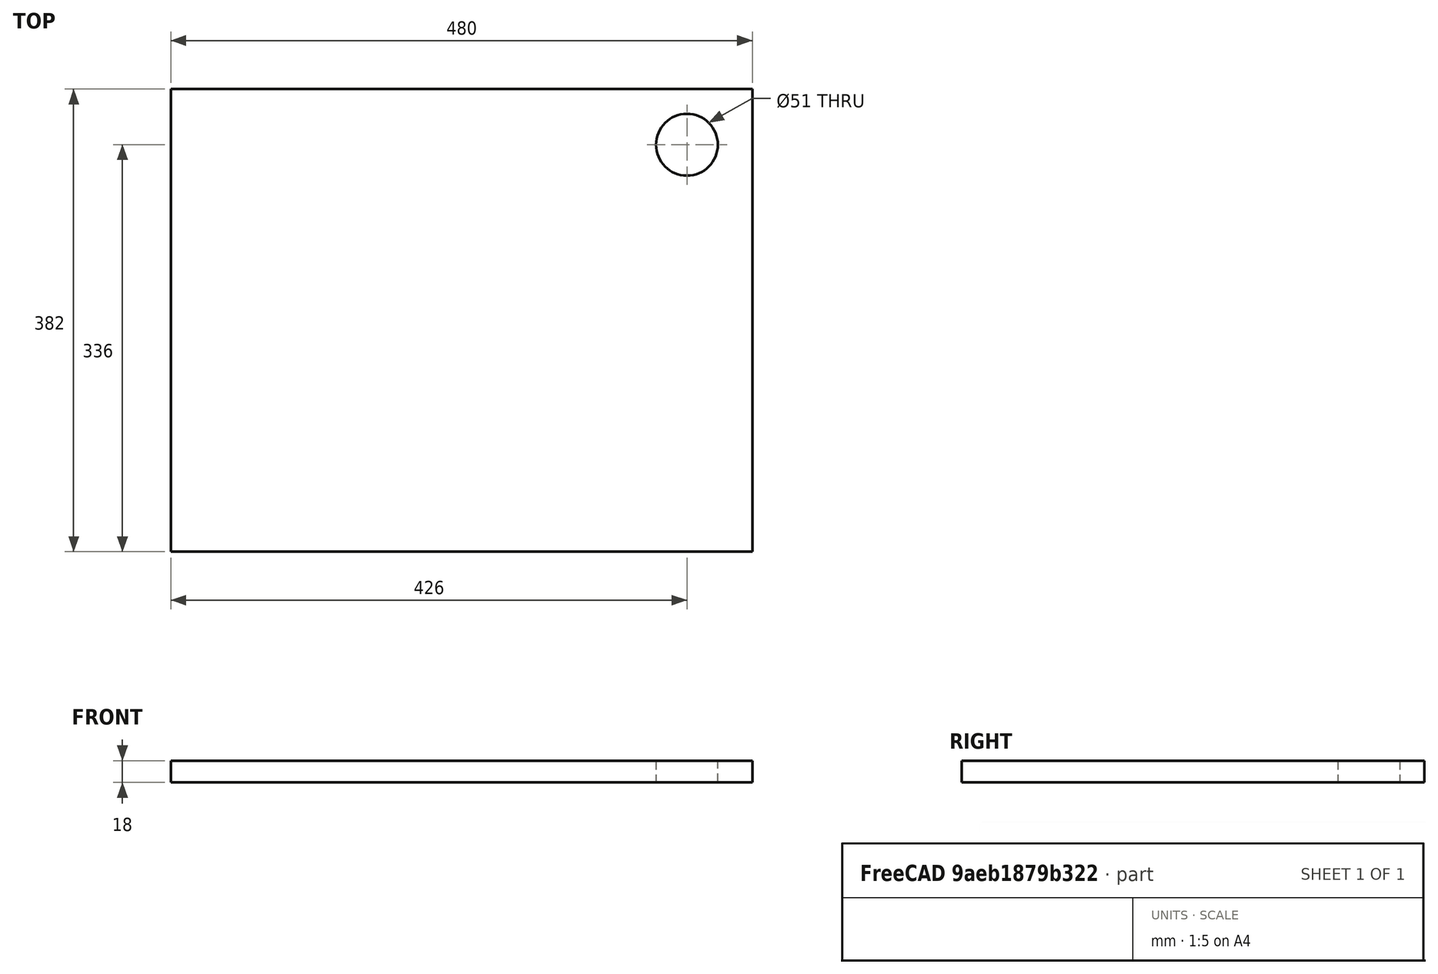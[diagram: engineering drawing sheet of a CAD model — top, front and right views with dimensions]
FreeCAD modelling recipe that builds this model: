
FCSTD DOCUMENT  (FreeCAD 0.18R4 (GitTag))
Label: horizontal_division
License: All rights reserved
LicenseURL: http://en.wikipedia.org/wiki/All_rights_reserved
objects: Sketcher::SketchObject×1, PartDesign::Pad×1, PartDesign::Body×1
note: 4 computed .brp shape members not serialized (recipe doc carries the construction recipe); baked Part::Feature solids carry a one-line shape summary decoded from their .brp

FEATURE [Sketcher::SketchObject] Sketch
  MapMode = 5
  Support = -> [XY_Plane]
  sketch-geometry (5):
    g0: LineSegment StartX=0 StartY=0 StartZ=0 EndX=-480 EndY=0 EndZ=0
    g1: LineSegment StartX=-480 StartY=0 StartZ=0 EndX=-480 EndY=382 EndZ=0
    g2: LineSegment StartX=-480 StartY=382 StartZ=0 EndX=0 EndY=382 EndZ=0
    g3: LineSegment StartX=0 StartY=382 StartZ=0 EndX=0 EndY=0 EndZ=0
    g4: Circle CenterX=-54 CenterY=336 CenterZ=0 NormalX=0 NormalY=0 NormalZ=1 AngleXU=0 Radius=25.5
  constraints (14):
    c: Coincident(g0,g1)
    c: Coincident(g1,g2)
    c: Coincident(g2,g3)
    c: Coincident(g3,g0)
    c: Horizontal(g0)
    c: Horizontal(g2)
    c: Vertical(g1)
    c: Vertical(g3)
    c: Coincident(g0,g-1)
    c: DistanceX(g0,g0) = 480
    c: DistanceY(g3,g3) = 382
    c: Diameter(g4) = 51
    c: DistanceX(g4,g2) = 54
    c: DistanceY(g4,g2) = 46
FEATURE [PartDesign::Pad] Pad
  Length = 18
  Length2 = 100
  Profile = -> Sketch
  Type = 0
FEATURE [PartDesign::Body] Body
  Group = -> [Sketch,Pad]
  Origin = -> Origin
  Tip = -> Pad
